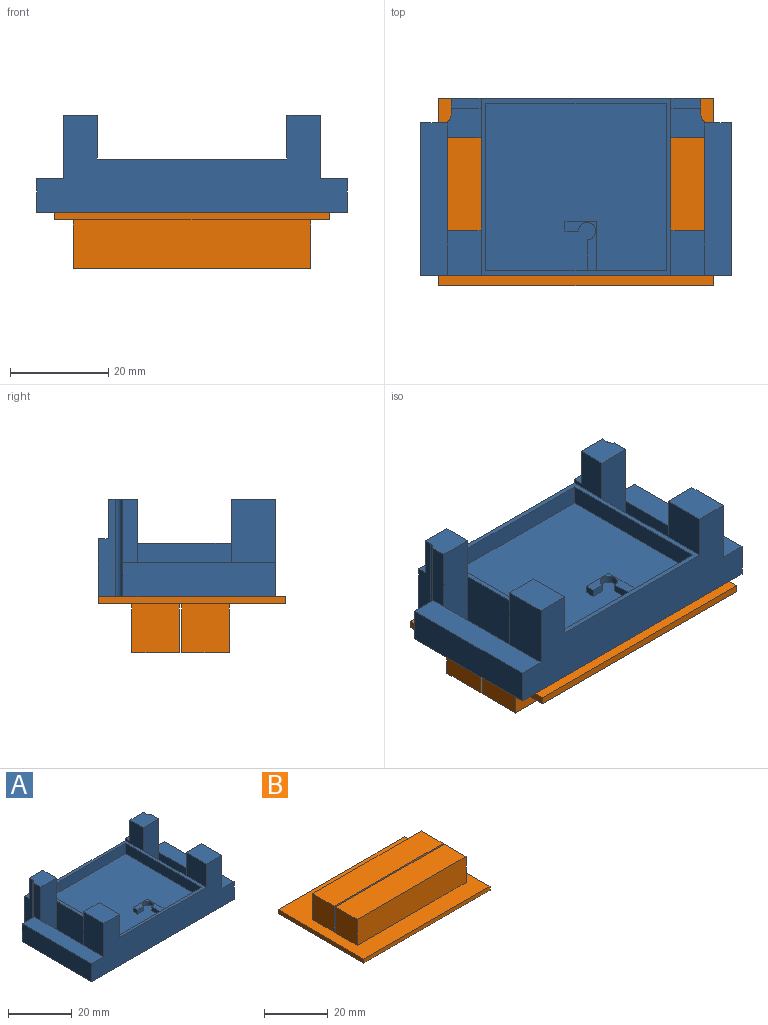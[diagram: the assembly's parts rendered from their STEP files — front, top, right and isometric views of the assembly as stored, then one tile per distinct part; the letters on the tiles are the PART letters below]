
ASSEMBLY  parts=2 mates=1
PART A: 50 faces, bbox 63.3x36x19.8 mm
  f0: plane 50.8x11.8mm, normal (0,1,0), area 564.7mm2, adj f2,f6,f7,f8,f32,f37,f46,f47
  f1: plane 12.9x3.2mm, normal (-1,0,0), area 41.2mm2, adj f3,f4,f21,f48
  f2: plane 63.25x36mm, normal (0,0,-1), area 1953.6mm2, adj f0,f16,f17,f18,f21,f22,f23,f24
  f3: plane 6.9x6mm, normal (0,0,1), area 39.4mm2, adj f1,f5,f7,f21,f46,f48
  f4: plane 31.2x5.4mm, normal (0,0,1), area 167.4mm2, adj f1,f11,f16,f18,f22,f30,f48
  f5: plane 8x6.08mm, normal (0,1,0), area 48.6mm2, adj f3,f6,f7,f46
  f6: plane 6.08x2mm, normal (0,0,1), area 12.1mm2, adj f0,f5,f7,f46
  f7: plane 8.9x8mm, normal (1,0,0), area 55.2mm2, adj f0,f3,f5,f6,f21,f37
  f8: plane 8.9x8mm, normal (-1,0,0), area 55.2mm2, adj f0,f15,f25,f31,f32,f37
  f9: plane 12.9x3.2mm, normal (1,0,0), area 41.2mm2, adj f10,f15,f25,f49
  f10: plane 31.2x5.4mm, normal (0,0,1), area 167.4mm2, adj f9,f14,f16,f17,f28,f29,f49
  f11: plane 12.9x9mm, normal (-1,0,0), area 116.1mm2, adj f4,f16,f19,f23
  f12: plane 9x8.9mm, normal (1,0,0), area 80.1mm2, adj f16,f19,f23,f37
  f13: plane 9x8.9mm, normal (-1,0,0), area 80.1mm2, adj f16,f20,f27,f37
  f14: plane 12.9x9mm, normal (1,0,0), area 116.1mm2, adj f10,f16,f20,f27
  f15: plane 6.9x6mm, normal (0,0,1), area 39.4mm2, adj f8,f9,f25,f31,f47,f49
  f16: plane 63.25x19.8mm, normal (0,-1,0), area 769mm2, adj f2,f4,f10,f11,f12,f13,f14,f17
  f17: plane 31x6.9mm, normal (1,0,0), area 213.9mm2, adj f2,f10,f16,f29
  f18: plane 31x6.9mm, normal (-1,0,0), area 213.9mm2, adj f2,f4,f16,f30
  f19: plane 9x6.9mm, normal (0,0,1), area 62.1mm2, adj f11,f12,f16,f23
  f20: plane 9x6.9mm, normal (0,0,1), area 62.1mm2, adj f13,f14,f16,f27
  f21: plane 19.8x6.9mm, normal (0,-1,0), area 136.6mm2, adj f1,f2,f3,f7,f22,f24
  f22: plane 19x6.9mm, normal (1,0,0), area 131.1mm2, adj f2,f4,f21,f23
  f23: plane 19.8x6.9mm, normal (0,1,0), area 136.6mm2, adj f2,f11,f12,f19,f22,f24
  f24: plane 19x10.9mm, normal (-1,0,0), area 207.1mm2, adj f2,f21,f23,f37
  f25: plane 19.8x6.9mm, normal (0,-1,0), area 136.6mm2, adj f2,f8,f9,f15,f26,f28
  f26: plane 19x10.9mm, normal (1,0,0), area 207.1mm2, adj f2,f25,f27,f37
  f27: plane 19.8x6.9mm, normal (0,1,0), area 136.6mm2, adj f2,f13,f14,f20,f26,f28
  f28: plane 19x6.9mm, normal (-1,0,0), area 131.1mm2, adj f2,f10,f25,f27
  f29: plane 6.9x4.64mm, normal (0,1,0), area 32mm2, adj f2,f10,f17,f49
  f30: plane 6.9x4.64mm, normal (0,1,0), area 32mm2, adj f2,f4,f18,f48
  f31: plane 8x6.08mm, normal (0,1,0), area 48.6mm2, adj f8,f15,f32,f47
  f32: plane 6.08x2mm, normal (0,0,1), area 12.1mm2, adj f0,f8,f31,f47
  f33: plane 36.65x4mm, normal (0,1,0), area 143.6mm2, adj f34,f35,f37,f42,f43,f44,f45
  f34: plane 34x4mm, normal (-1,0,0), area 136mm2, adj f33,f36,f37,f45
  f35: plane 34x4mm, normal (1,0,0), area 136mm2, adj f33,f36,f37,f45
  f36: plane 36.65x4mm, normal (0,-1,0), area 146.6mm2, adj f34,f35,f37,f45
  f37: plane 38.65x36mm, normal (0,0,1), area 145.3mm2, adj f0,f7,f8,f12,f13,f16,f24,f26
  f38: cylinder r=1.75mm len=3.5mm, axis (0,0,-1), area 12.4mm2, adj f39,f42,f43,f45
  f39: plane 2.75x1.5mm, normal (0,-1,0), area 4.1mm2, adj f38,f40,f42,f45
  f40: plane 2x1.5mm, normal (-1,0,0), area 3mm2, adj f39,f41,f42,f45
  f41: plane 6.5x1.5mm, normal (0,1,0), area 9.8mm2, adj f40,f42,f44,f45
  f42: plane 10x6.5mm, normal (0,0,1), area 21.8mm2, adj f33,f38,f39,f40,f41,f43,f44
  f43: plane 6.25x1.5mm, normal (-1,0,0), area 9.4mm2, adj f33,f38,f42,f45
  f44: plane 10x1.5mm, normal (1,0,0), area 15mm2, adj f33,f41,f42,f45
  f45: plane 36.65x34mm, normal (0,0,1), area 1224.3mm2, adj f33,f34,f35,f36,f38,f39,f40,f41
  f46: plane 19.8x3.41mm, normal (-1,0,0), area 51.6mm2, adj f0,f2,f3,f5,f6,f48
  f47: plane 19.8x3.41mm, normal (1,0,0), area 51.6mm2, adj f0,f2,f15,f31,f32,f49
  f48: cylinder r=1.59mm len=19.8mm, axis (0,0,1), area 39.1mm2, adj f1,f2,f3,f4,f30,f46
  f49: cylinder r=1.59mm len=19.8mm, axis (0,0,1), area 39.1mm2, adj f2,f9,f10,f15,f29,f47
PART B: 16 faces, bbox 55.9x38.1x11.4 mm
  f0: plane 55.88x1.5mm, normal (0,1,0), area 83.8mm2, adj f1,f3,f4,f5
  f1: plane 38.1x1.5mm, normal (-1,0,0), area 57.1mm2, adj f0,f2,f4,f5
  f2: plane 55.88x1.5mm, normal (0,-1,0), area 83.8mm2, adj f1,f3,f4,f5
  f3: plane 38.1x1.5mm, normal (1,0,0), area 57.1mm2, adj f0,f2,f4,f5
  f4: plane 55.88x38.1mm, normal (0,0,1), area 1197.4mm2, adj f0,f1,f2,f3,f7,f8,f9,f10
  f5: plane 55.88x38.1mm, normal (0,0,-1), area 2129mm2, adj f0,f1,f2,f3
  f6: plane 48.26x9.65mm, normal (0,0,1), area 465.8mm2, adj f7,f8,f9,f10
  f7: plane 9.93x9.65mm, normal (1,0,0), area 95.8mm2, adj f4,f6,f8,f10
  f8: plane 48.26x9.93mm, normal (0,-1,0), area 479.2mm2, adj f4,f6,f7,f9
  f9: plane 9.93x9.65mm, normal (-1,0,0), area 95.8mm2, adj f4,f6,f8,f10
  f10: plane 48.26x9.93mm, normal (0,1,0), area 479.2mm2, adj f4,f6,f7,f9
  f11: plane 48.26x9.65mm, normal (0,0,1), area 465.8mm2, adj f12,f13,f14,f15
  f12: plane 9.93x9.65mm, normal (1,0,0), area 95.8mm2, adj f4,f11,f13,f15
  f13: plane 48.26x9.93mm, normal (0,-1,0), area 479.2mm2, adj f4,f11,f12,f14
  f14: plane 9.93x9.65mm, normal (-1,0,0), area 95.8mm2, adj f4,f11,f13,f15
  f15: plane 48.26x9.93mm, normal (0,1,0), area 479.2mm2, adj f4,f11,f12,f14
PLACE A t=(-1.3,-14.17,22.58)mm
PLACE B rot(axis=(1,0,0),180deg) t=(-4.99,21.83,22.58)mm
MATE fastened A.f0 <-> B.f2  axis (0,1,0) through (-32.93,21.83,22.58)mm
